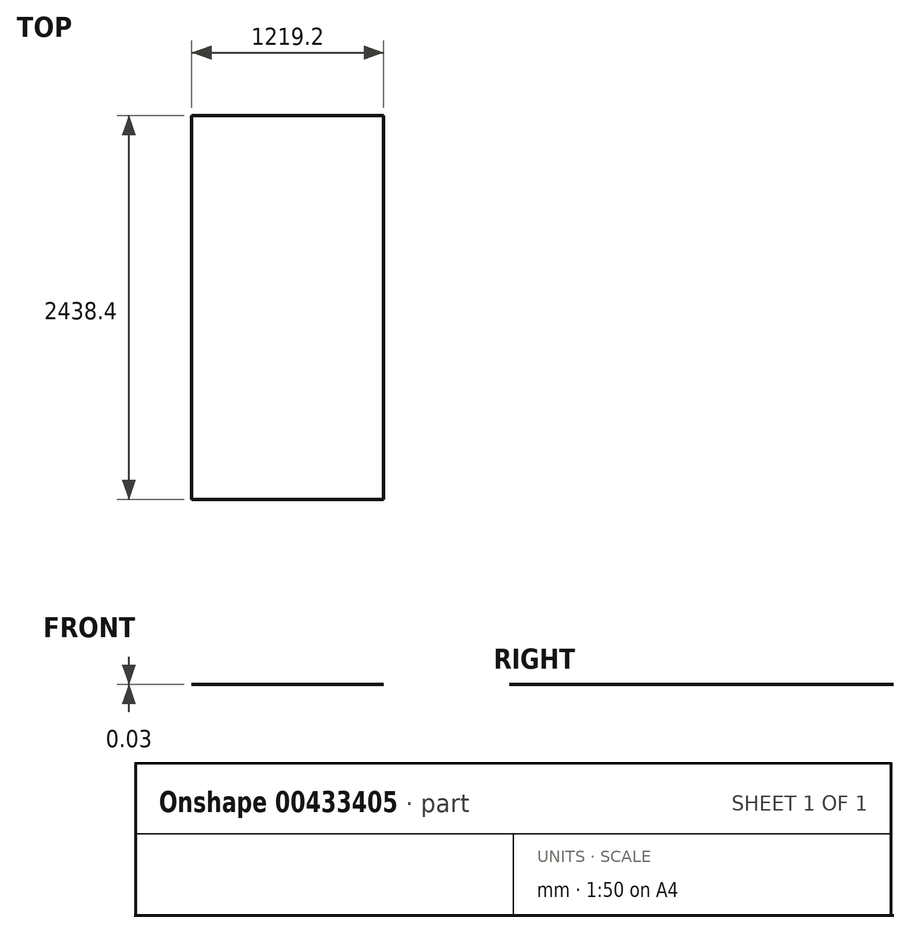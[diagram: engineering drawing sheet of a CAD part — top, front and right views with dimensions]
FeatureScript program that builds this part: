
annotation { "Feature Type Name" : "Feature", "Feature Type Description" : "" }
export const myFeature = defineFeature(function(context is Context, id is Id, definition is map)
    precondition{}
    {
        {
            var Q0;
            Q0=qCreatedBy(makeId("Top.planeOp"),FACE);
            var sketch = newSketch(context, id + "F0", { "sketchPlane" : qUnion([Q0])});
            skLineSegment(sketch, "E0.bottom", {"start": v(0, 0) * mm, "end": v(1219.2, 0) * mm});
            skLineSegment(sketch, "E0.top", {"start": v(0, 2438.4) * mm, "end": v(1219.2, 2438.4) * mm});
            skLineSegment(sketch, "E0.left", {"start": v(0, 0) * mm, "end": v(0, 2438.4) * mm});
            skLineSegment(sketch, "E0.right", {"start": v(1219.2, 0) * mm, "end": v(1219.2, 2438.4) * mm});
            skSolve(sketch);
        }
        {
            var Q0;
            Q0 = qSketchRegion(id + "F0", true);
            extrude(context, id + "F1", {"entities" : qUnion([Q0]), "depth" : 0.03 * mm, "offsetDistance" : 25.4 * mm});
        }
    });
